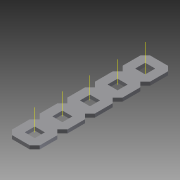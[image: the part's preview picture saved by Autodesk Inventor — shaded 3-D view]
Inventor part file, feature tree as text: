
AUTODESK INVENTOR PART (.ipt)
format: ipt  version: 2015 (Build 190159000, 159)  size: 1,059,328 bytes
history: native  units: in
note: dims shown in document units (in); Inventor stores cm internally (conversion verified against a paired STEP export)
features: other x14, extrude x2, pattern_linear x1, imported_body x1
ambient origin geometry x8: Origin, YZ Plane, XZ Plane, XY Plane, X Axis, Y Axis, Z Axis, Center Point
bodies: Body1 (feature_tree)
feature tree (18):
  other  "Diamond-Pattern"
  other  "Plate"
  extrude  "length cut"  TaperAngle=0.0deg  [1 undecoded]
  extrude  "width cut"  TaperAngle=0.0deg  [1 undecoded]
  other  "constraint axis"
  pattern_linear  "constraint axes"  Spacing1=0.5in  [1 undecoded]
  other  "front plane"
  other  "right plane"
  imported_body  "Base1"
  other  "length profile"
  other  "width profile"
  other  "Work Point1"
  other  "back plane"
  other  "left plane"
  other  "Work Axis170"
  other  "Work Axis171"
  other  "Work Axis172"
  other  "Work Axis173"
note: 3 required parameter values undecoded (feature->parameter linkage not recoverable at this tier; creation-order binding heuristic only, values carry confidence <= 0.55)
